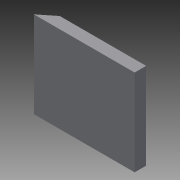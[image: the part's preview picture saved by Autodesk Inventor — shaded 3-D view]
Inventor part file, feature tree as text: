
AUTODESK INVENTOR PART (.ipt)
format: ipt  version: 2015 (Build 190159000, 159)  size: 87,040 bytes
history: native  units: in
note: dims shown in document units (in); Inventor stores cm internally (conversion verified against a paired STEP export)
features: extrude x1, sketch x1
ambient origin geometry x8: Origin, YZ Plane, XZ Plane, XY Plane, X Axis, Y Axis, Z Axis, Center Point
bodies: Solid1 (feature_tree)
feature tree (2):
  extrude  "Extrusion1"  Depth=1.1811in
  sketch  "Sketch1"  dims[d0=0.6299in d1=1.1811in d2=0.1575in d3=1.9685in d4=1.9685in d5=0.5906in d6=0.0787in d7=0.1969in d8=0.9843in d9=0.1969in d10=0.1969in d11=0.5906in d12=1.1811in d13=0.0in]
